# Revit family: Adaptateur 8 MTP
name_source: partatom
category: Installations électriques
units: mm (PartAtom-declared; Revit-internal decimal feet)

## family parameters
Basée sur le plan de construction = Non
Conserver l'orientation des annotations = Non
Cote de connecteur circulaire = Utiliser le diamètre
Couper avec des vides une fois chargée = Non
Partagée = Non
Point de calcul de pièce = Non
Toujours verticalement = Oui
Type d'élément = Normal

## types (2) — shared parameters
Classe ETIM = EC001130
Couleur = IDS_NOIR
Fonction = Panneaux fibre optique HD Legrand
Hauteur = 23 mm  [stored 0.0754593 ft]
Hauteur de l'ouverture = 1 mm  [stored 0.00328084 ft]
Hauteur des connecteurs = 10 mm  [stored 0.0328084 ft]
IK = IK04
IP = IP20
Largeur (mm) = 109 mm
Largeur de l'ouverture = 8.35 mm  [stored 0.027395 ft]
Largeur des connecteurs = 13.5 mm  [stored 0.0442913 ft]
Lien e-catalogue = https://www.legrand.fr
Nombre de connecteurs = 8
Profondeur = 45 mm
RAL = 9001
Température de fonctionnement = -10°C à 60°C
Température de stockage = -10°C à 60°C
Type de connecteur externe = MT_MPO
Type de connecteur interne = MT_MPO
zero-valued in all types: Elévation par défaut

## per-type parameters (varying)
| type | Couleur des connecteurs | EAN | Référence Legrand | Type de fibre optique |
| Adaptateur 8 MTP traversée multimode | IDS_JAUNE | 3414971929234 | 032118 | Multimode |
| Adaptateur 8 MTP traversée monomode | IDS_VERT | 3414971929241 | 032119 | Monomode |

note: column(s) folded — value = type name in every type: Libellé BIM

note: [stored X ft] marks values corroborated as IEEE doubles in the binary element streams (Revit-internal decimal feet)
